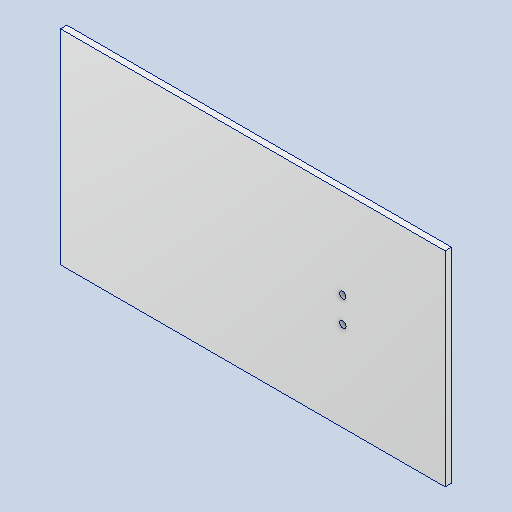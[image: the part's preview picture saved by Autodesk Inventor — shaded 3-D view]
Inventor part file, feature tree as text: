
AUTODESK INVENTOR PART (.ipt)
format: ipt  version: 2023.2 (Build 272271000, 271)  size: 105,472 bytes
history: native  units: mm
features: reference x4, other x4, extrude x2, sketch x2
ambient origin geometry x8: Origin, YZ Plane, XZ Plane, XY Plane, X Axis, Y Axis, Z Axis, Center Point
bodies: Solid1 (feature_tree)
feature tree (12):
  extrude  "Extrusion1"  Depth=5.0mm
  extrude  "Extrusion2"  [1 undecoded]
  sketch  "Sketch1"  dims[d0=5.0mm d1=0.0mm d3=60.0mm]
  reference  "Reference1"
  reference  "Reference2"
  sketch  "Sketch2"  dims[d4=0.0mm d5=0.0mm]
  reference  "Reference3"
  reference  "Reference4"
  parser-record x1  (decoder bookkeeping rows leaked as tree rows — omitted from the tree; the rows remain in map.json)
  other  "Main Assembly.iam"
  other  "V Rail Gantry:1"
  other  "8mm Acme Anti Backlash Nut Block:1"
note: 1 required parameter value undecoded (feature->parameter linkage not recoverable at this tier; creation-order binding heuristic only, values carry confidence <= 0.55)
note: 1 file-system path scrubbed to <path> (originals preserved in map.json)
